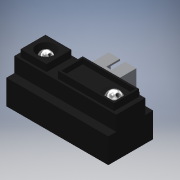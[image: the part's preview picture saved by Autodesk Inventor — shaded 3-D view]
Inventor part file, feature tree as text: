
AUTODESK INVENTOR PART (.ipt)
format: ipt  version: 2016 (Build 200138000, 138)  size: 445,440 bytes
history: native  units: mm
features: extrude x19, sketch x14, plane x3, mirror x3, revolve x3, loft x2, projected_geometry x2
ambient origin geometry x8: Origin, YZ Plane, XZ Plane, XY Plane, X Axis, Y Axis, Z Axis, Center Point
bodies: Solid1 (feature_tree)
feature tree (46):
  extrude  "Extrusion1"  Depth=13.0mm
  extrude  "Extrusion2"  Depth=4.2mm
  extrude  "Extrusion3"  Depth=6.3mm TaperAngle=0.0deg
  extrude  "Extrusion4"  Depth=7.2mm
  extrude  "Extrusion5"  Depth=1.2mm
  extrude  "Extrusion6"  Depth=2.0mm TaperAngle=0.0deg
  extrude  "Extrusion7"  Depth=7.5mm
  sketch  "Sketch8"  dims[d2=13.5mm d3=0.0mm d4=4.2mm]
  sketch  "Sketch9"  dims[d5=8.4mm d6=6.3mm d7=0.0mm]
  plane  "Work Plane1"
  extrude  "Extrusion8"  Depth=6.3mm TaperAngle=0.0deg
  extrude  "Extrusion9"  Depth=3.2mm
  plane  "Work Plane2"
  mirror  "Mirror1"
  loft  "Loft1"
  sketch  "Sketch14"  dims[d13=1.2mm d14=2.0mm d15=0.0mm]
  plane  "Work Plane3"
  revolve  "Revolution1"  [1 undecoded]
  revolve  "Revolution2"  [1 undecoded]
  extrude  "Extrusion10"  Depth=3.5mm
  loft  "Loft2"
  extrude  "Extrusion11"  TaperAngle=0.0deg  [1 undecoded]
  revolve  "Revolution3"  Angle=90.0deg
  extrude  "Extrusion12"  TaperAngle=90.0deg  [1 undecoded]
  extrude  "Extrusion13"  Depth=0.5mm
  mirror  "Mirror2"
  extrude  "Extrusion14"  Depth=0.5mm
  extrude  "Extrusion15"  Depth=0.5mm
  mirror  "Mirror3"
  extrude  "Extrusion16"  Depth=0.5mm
  extrude  "Extrusion17"  Depth=1.5mm TaperAngle=0.0deg
  extrude  "Wyciągnięcie proste18"  Depth=6.2mm
  extrude  "Wyciągnięcie proste19"  Depth=4.2mm
  sketch  "Sketch7"  dims[d0=29.5mm d1=13.0mm]
  sketch  "Sketch12"  dims[d8=3.6mm d9=7.2mm]
  sketch  "Sketch13"  dims[d10=2.0mm d11=0.0mm d12=1.2mm]
  sketch  "Sketch15"  dims[d16=16.3mm d17=7.5mm]
  sketch  "Sketch17"  dims[d18=2.0mm d19=0.0mm d20=6.3mm d21=0.0mm]
  sketch  "Sketch18"  dims[d22=3.75mm d23=3.2mm]
  projected_geometry  "Projected Loop1"
  projected_geometry  "Projected Loop2"
  sketch  "Sketch22"  dims[d24=1.5mm d25=0.0mm d26=2.6mm]
  sketch  "Sketch24"  dims[d27=5.0mm d28=1.5mm d29=0.0mm]
  sketch  "Sketch26"  dims[d30=1.5mm d31=0.0mm d32=1.0mm d33=3.5mm d34=0.0mm d35=90.0deg d36=0.0mm d37=90.0deg d38=90.0deg d39=90.0deg d40=0.5mm d41=0.5mm d42=0.5mm d43=0.5mm d44=1.5mm d45=0.0mm d46=6.2mm d47=4.2mm d48=0.0mm d49=90.0deg d50=0.0mm d51=90.0deg d52=0.5mm d53=0.0mm d54=90.0deg d55=3.3mm d56=5.05mm d57=10.1mm d58=5.9mm d59=0.0mm d60=4.0mm d61=5.3mm d62=0.0mm d65=0.5mm d66=0.5mm d67=4.5mm d68=0.0mm d69=2.0mm d70=0.7mm d71=0.5mm d72=0.0mm d73=0.75mm d74=4.0mm d75=1.5mm d76=0.5mm d77=0.0mm d78=45.0deg d79=0.5mm d80=0.5mm d81=3.3mm d82=0.0mm d85=10.0mm d86=0.0mm d87=10.0mm d88=0.0mm]
  sketch  "Szkic28"
  sketch  "Szkic29"
note: 4 required parameter values undecoded (feature->parameter linkage not recoverable at this tier; creation-order binding heuristic only, values carry confidence <= 0.55)